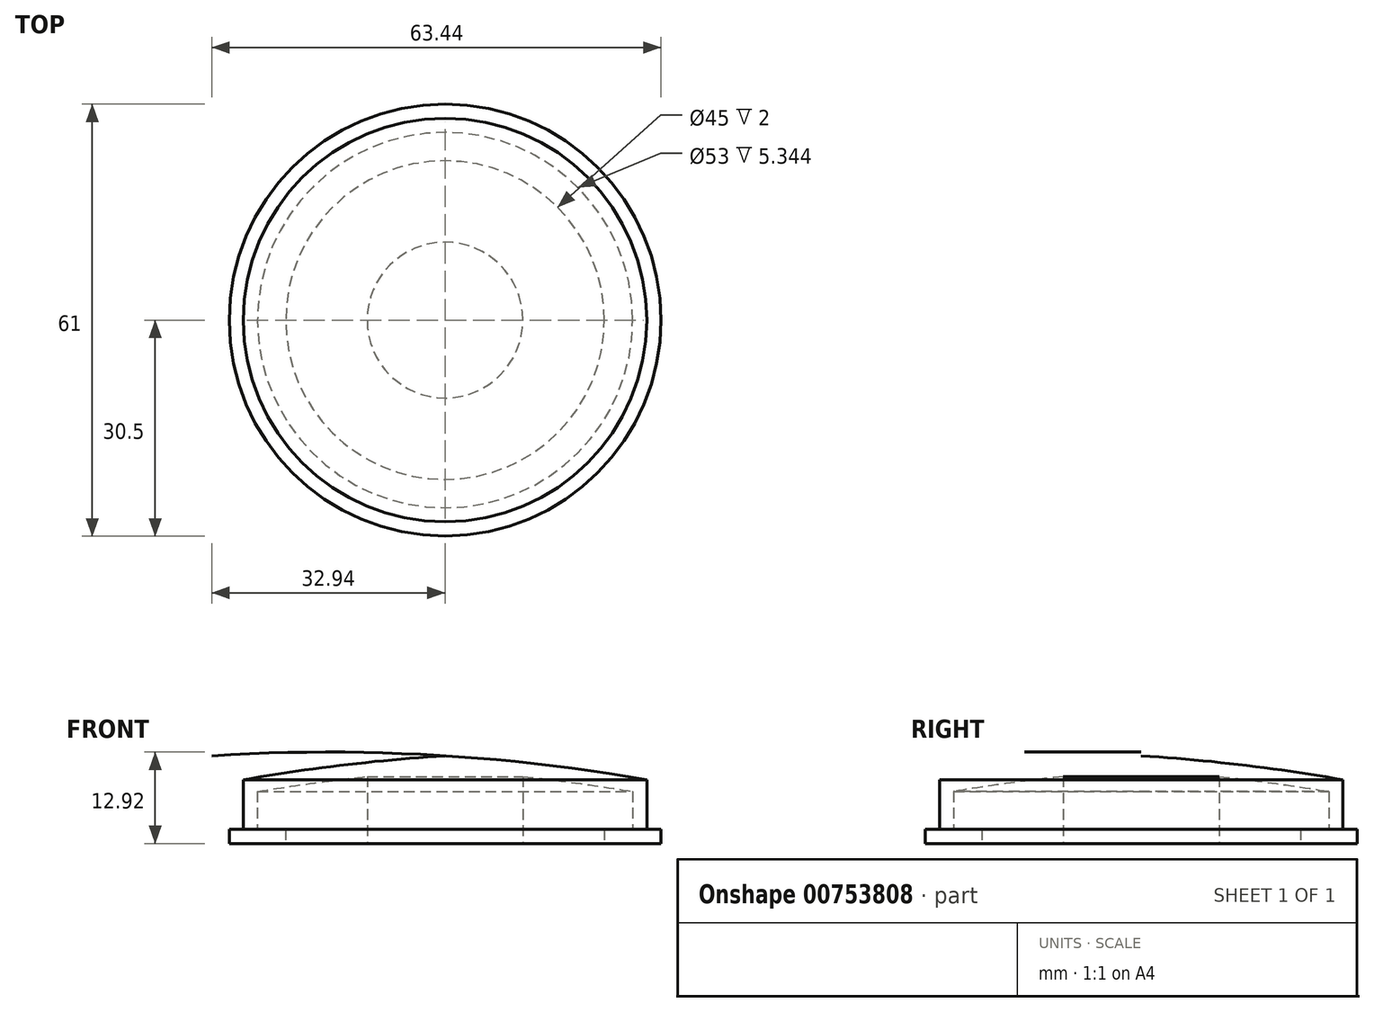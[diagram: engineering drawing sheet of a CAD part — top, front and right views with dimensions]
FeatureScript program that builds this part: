
annotation { "Feature Type Name" : "Feature", "Feature Type Description" : "" }
export const myFeature = defineFeature(function(context is Context, id is Id, definition is map)
    precondition{}
    {
        {
            var Q0;
            Q0=qCreatedBy(makeId("Front.planeOp"),FACE);
            var sketch = newSketch(context, id + "F0", { "sketchPlane" : qUnion([Q0])});
            skLineSegment(sketch, "E0", {"start": v(0, 0) * mm, "end": v(26.5, 0) * mm});
            skLineSegment(sketch, "E1", {"start": v(26.5, 0) * mm, "end": v(28.5, 0) * mm});
            skLineSegment(sketch, "E2", {"start": v(28.5, 0) * mm, "end": v(30.5, 0) * mm});
            skLineSegment(sketch, "E3", {"start": v(30.5, 0) * mm, "end": v(30.5, 2) * mm});
            skLineSegment(sketch, "E4", {"start": v(30.5, 2) * mm, "end": v(28.5, 2) * mm});
            skLineSegment(sketch, "E5", {"start": v(28.5, 2) * mm, "end": v(28.5, 7) * mm});
            skLineSegment(sketch, "E6", {"start": v(0, 0) * mm, "end": v(0, 10.4) * mm});
            skArc(sketch, "E7", {"start": v(26.5, 7.34) * mm, "mid": v(18.77, 8.52) * mm, "end": v(11, 9.47) * mm});
            skLineSegment(sketch, "E8", {"start": v(0, 10.4) * mm, "end": v(0, 12.4) * mm});
            skLineSegment(sketch, "E9", {"start": v(28.5, 7) * mm, "end": v(28.5, 9) * mm});
            skArc(sketch, "E10", {"start": v(28.5, 9) * mm, "mid": v(14.3, 11.1) * mm, "end": v(0, 12.4) * mm});
            skLineSegment(sketch, "E11", {"start": v(26.5, 2) * mm, "end": v(26.5, 7.34) * mm});
            skLineSegment(sketch, "E12", {"start": v(0, 0) * mm, "end": v(9, 0) * mm});
            skLineSegment(sketch, "E13", {"start": v(9, 0) * mm, "end": v(11, 0) * mm});
            skLineSegment(sketch, "E14", {"start": v(11, 0) * mm, "end": v(11, 9.47) * mm});
            skLineSegment(sketch, "E15", {"start": v(26.5, 0) * mm, "end": v(22.5, 0) * mm});
            skLineSegment(sketch, "E16", {"start": v(22.5, 0) * mm, "end": v(22.5, 2) * mm});
            skLineSegment(sketch, "E17", {"start": v(22.5, 2) * mm, "end": v(26.5, 2) * mm});
            skPoint(sketch, "E18.orphan", {"position": v(9, 12.92) * mm});
            skSolve(sketch);
        }
        {
            var Q0;
            Q0=makeQuery(id+"F0.imprint","IMPRINT",FACE,{"disambiguationData":[TD([[makeQuery(id+"F0.imprint","IMPRINT",EDGE,{"derivedFrom":sQuery(id+"F0.wireOp",EDGE,"E1")}),1.0]])]});
            var Q1;
            Q1=sQuery(id+"F0.wireOp",EDGE,"E8");
            revolve(context, id + "F1", {"surfaceOperationType" : NewSurfaceOperationType.NEW, "entities" : qUnion([Q0]), "axis" : qUnion([Q1]), "revolveType" : RevolveType.FULL});
        }
    });
